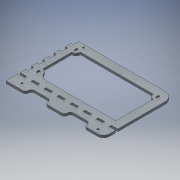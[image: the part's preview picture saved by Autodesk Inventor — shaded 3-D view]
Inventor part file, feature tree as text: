
AUTODESK INVENTOR PART (.ipt)
format: ipt  version: 2018.3 (Build 223284000, 284)  size: 248,320 bytes
history: native  units: mm
features: reference x16, other x5, extrude x3, fillet x2, sketch x2
ambient origin geometry x8: Origin, YZ Plane, XZ Plane, XY Plane, X Axis, Y Axis, Z Axis, Center Point
bodies: Solido1 (feature_tree)
feature tree (28):
  extrude  "Estrusione1"  Depth=165.0mm
  extrude  "Estrusione2"  Depth=33.0mm
  fillet  "Raccordo1"  Radius=10.0mm
  fillet  "Raccordo2"  Radius=33.0mm
  extrude  "Estrusione3"  Depth=10.0mm
  sketch  "Schizzo1"
  reference  "Riferimento4"
  reference  "Riferimento5"
  reference  "Riferimento6"
  reference  "Riferimento8"
  reference  "Riferimento9"
  reference  "Riferimento10"
  reference  "Riferimento11"
  reference  "Riferimento12"
  reference  "Riferimento13"
  reference  "Riferimento14"
  reference  "Riferimento15"
  sketch  "Schizzo2"
  reference  "Riferimento16"
  reference  "Riferimento17"
  reference  "Riferimento18"
  reference  "Riferimento19"
  reference  "Riferimento20"
  other  "<userpath>\Desktop\Scorbot Hardware\Case Board V2\caseHw v2.iam"
  other  "caseHw v2.iam"
  other  "LC600H-12:1"
  other  "tavolaBase:1"
  other  "Dietro:1"
